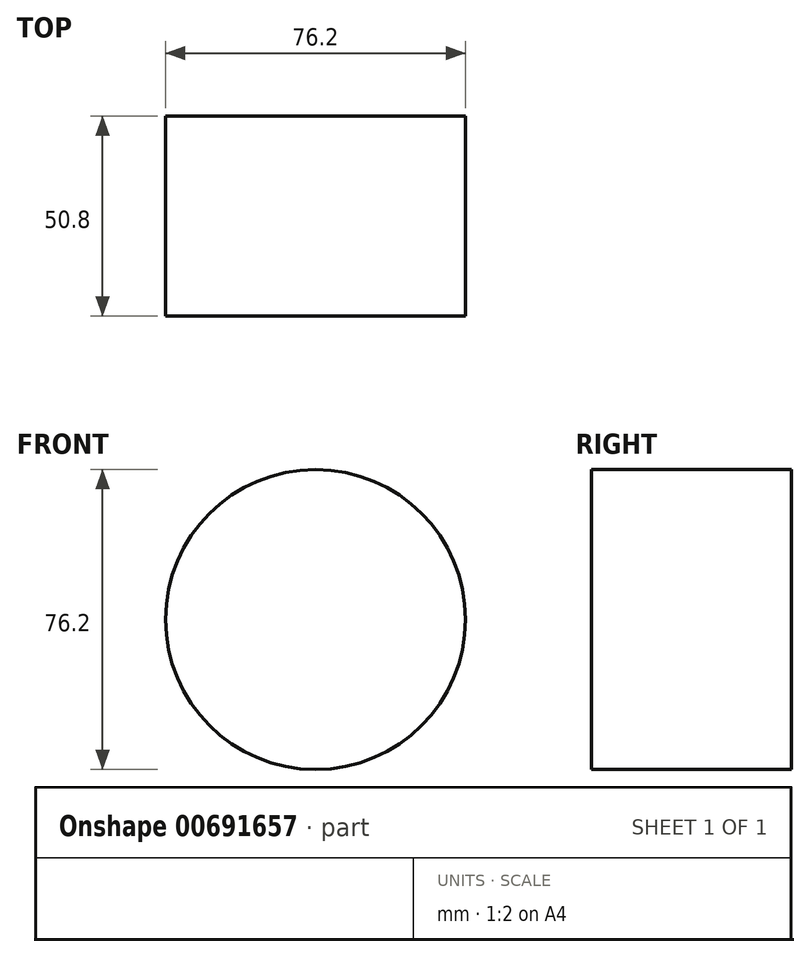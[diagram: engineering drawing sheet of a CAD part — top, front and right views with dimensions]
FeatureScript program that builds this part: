
annotation { "Feature Type Name" : "Feature", "Feature Type Description" : "" }
export const myFeature = defineFeature(function(context is Context, id is Id, definition is map)
    precondition{}
    {
        {
            var Q0;
            Q0=qCreatedBy(makeId("Front.planeOp"),FACE);
            var sketch = newSketch(context, id + "F0", { "sketchPlane" : qUnion([Q0])});
            skCircle(sketch, "E0", {"center": v(0, 0) * mm, "radius": 38.1 * mm});
            skSolve(sketch);
        }
        {
            var Q0;
            Q0=makeQuery(id+"F0.imprint","IMPRINT",FACE,{"disambiguationData":[TD([[makeQuery(id+"F0.imprint","IMPRINT",EDGE,{"derivedFrom":sQuery(id+"F0.wireOp",EDGE,"E0")}),1.0]])]});
            extrude(context, id + "F1", {"entities" : qUnion([Q0]), "depth" : 12.7 * mm, "offsetDistance" : 25.4 * mm});
        }
        {
            var Q0;
            Q0=makeQuery(id+"F1.opExtrude","CAP_FACE",FACE,{"disambiguationData":[OSD([sQuery(id+"F0.wireOp",EDGE,"E0")])],"isStart":false});
            extrude(context, id + "F2", {"entities" : qUnion([Q0]), "operationType" : NewBodyOperationType.ADD, "depth" : 25.4 * mm, "offsetDistance" : 25.4 * mm});
        }
        {
            var Q0;
            Q0=makeQuery(id+"F2.opExtrude","CAP_FACE",FACE,{"disambiguationData":[OSD([sQuery(id+"F0.wireOp",EDGE,"E0")])],"isStart":false});
            extrude(context, id + "F3", {"entities" : qUnion([Q0]), "operationType" : NewBodyOperationType.ADD, "depth" : 12.7 * mm, "offsetDistance" : 25.4 * mm});
        }
        {
            var Q0;
            Q0=qCreatedBy(makeId("Front.planeOp"),FACE);
            var sketch = newSketch(context, id + "F4", { "sketchPlane" : qUnion([Q0])});
            skLineSegment(sketch, "E1", {"start": v(0, 39.12) * mm, "end": v(99.64, 56.54) * mm});
            skLineSegment(sketch, "E2", {"start": v(0, -38.23) * mm, "end": v(99.64, -55.65) * mm});
            skLineSegment(sketch, "E3", {"start": v(99.64, -55.65) * mm, "end": v(99.64, 56.54) * mm});
            skSolve(sketch);
        }
        {
            var Q0;
            Q0=sQuery(id+"F4.wireOp",EDGE,"E1");
            var Q1;
            Q1=sQuery(id+"F4.wireOp",EDGE,"E3");
            var Q2;
            Q2=sQuery(id+"F4.wireOp",EDGE,"E2");
            extrude(context, id + "F5", {"bodyType" : ToolBodyType.SURFACE, "surfaceEntities" : qUnion([Q0, Q1, Q2]), "depth" : 37.08 * mm, "offsetDistance" : 25.4 * mm, "hasSecondDirection" : true, "secondDirectionOppositeDirection" : false, "secondDirectionDepth" : 7.37 * mm});
        }
    });
